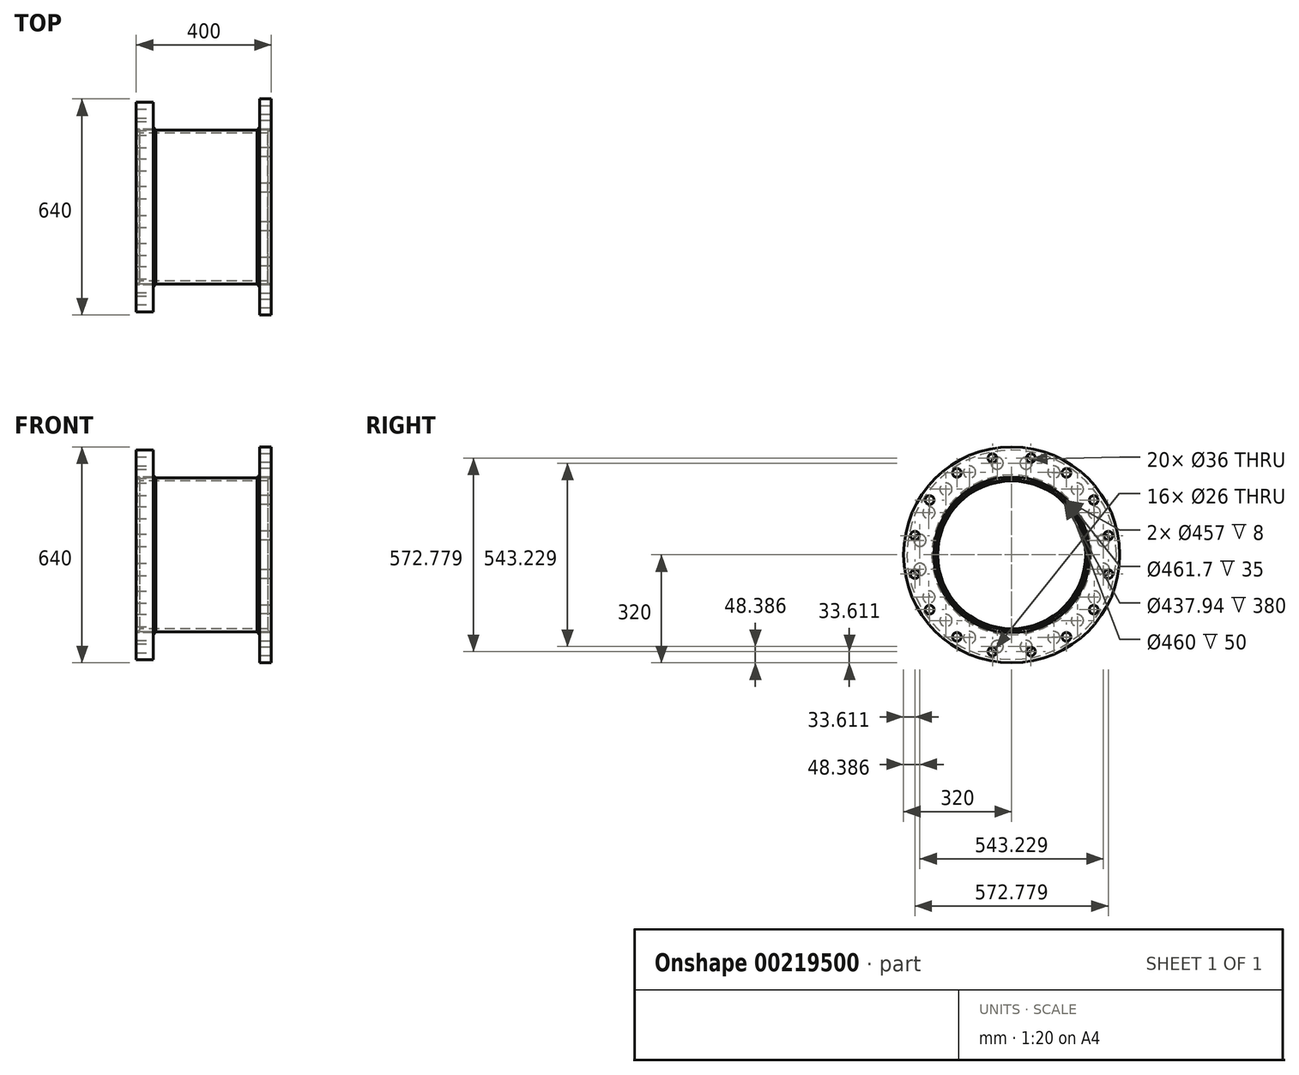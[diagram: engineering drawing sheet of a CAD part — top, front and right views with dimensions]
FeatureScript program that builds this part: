
annotation { "Feature Type Name" : "Feature", "Feature Type Description" : "" }
export const myFeature = defineFeature(function(context is Context, id is Id, definition is map)
    precondition{}
    {
        {
            var Q0;
            Q0=qCreatedBy(makeId("Front.planeOp"),FACE);
            var sketch = newSketch(context, id + "F0", { "sketchPlane" : qUnion([Q0])});
            skLineSegment(sketch, "E0", {"start": v(-189.34, 0) * mm, "end": v(169, 0) * mm, "construction": true});
            skLineSegment(sketch, "E1.bottom", {"start": v(0, 218.97) * mm, "end": v(-190, 218.97) * mm});
            skLineSegment(sketch, "E1.top", {"start": v(0, 228.5) * mm, "end": v(-190, 228.5) * mm});
            skLineSegment(sketch, "E1.left", {"start": v(0, 218.97) * mm, "end": v(0, 228.5) * mm});
            skLineSegment(sketch, "E1.right", {"start": v(-190, 218.97) * mm, "end": v(-190, 228.5) * mm});
            skLineSegment(sketch, "E2.bottom", {"start": v(-150, 230) * mm, "end": v(-200, 230) * mm});
            skLineSegment(sketch, "E2.top", {"start": v(-150, 310) * mm, "end": v(-200, 310) * mm});
            skLineSegment(sketch, "E2.left", {"start": v(-150, 230) * mm, "end": v(-150, 310) * mm});
            skLineSegment(sketch, "E2.right", {"start": v(-200, 230) * mm, "end": v(-200, 310) * mm});
            skLineSegment(sketch, "E3", {"start": v(0, 356.96) * mm, "end": v(0, -269.86) * mm, "construction": true});
            skLineSegment(sketch, "E4.MirrorCS", {"start": v(0, 228.5) * mm, "end": v(190, 228.5) * mm});
            skLineSegment(sketch, "E5.MirrorCS", {"start": v(0, 218.97) * mm, "end": v(190, 218.97) * mm});
            skLineSegment(sketch, "E6.MirrorCS", {"start": v(190, 218.97) * mm, "end": v(190, 228.5) * mm});
            skLineSegment(sketch, "E7.bottom", {"start": v(165, 230.85) * mm, "end": v(200, 230.85) * mm});
            skLineSegment(sketch, "E7.top", {"start": v(165, 320) * mm, "end": v(200, 320) * mm});
            skLineSegment(sketch, "E7.left", {"start": v(165, 230.85) * mm, "end": v(165, 320) * mm});
            skLineSegment(sketch, "E7.right", {"start": v(200, 230.85) * mm, "end": v(200, 320) * mm});
            skLineSegment(sketch, "E8", {"start": v(-198, 230) * mm, "end": v(-190, 222) * mm});
            skLineSegment(sketch, "E9", {"start": v(-190, 230) * mm, "end": v(-190, 228.5) * mm});
            skLineSegment(sketch, "E10", {"start": v(190, 228.5) * mm, "end": v(190, 230.85) * mm});
            skLineSegment(sketch, "E11", {"start": v(198, 230.85) * mm, "end": v(190, 222.85) * mm});
            skLineSegment(sketch, "E12", {"start": v(165, 230.85) * mm, "end": v(165, 228.5) * mm});
            skLineSegment(sketch, "E13", {"start": v(165, 236.5) * mm, "end": v(157, 228.5) * mm});
            skLineSegment(sketch, "E14", {"start": v(-150, 236.5) * mm, "end": v(-142, 228.5) * mm});
            skLineSegment(sketch, "E15", {"start": v(-150, 230) * mm, "end": v(-150, 228.5) * mm});
            skSolve(sketch);
        }
        {
            var Q0;
            {var subQ0=sQuery(id+"F0.wireOp",EDGE,"E2.top");Q0=makeQuery(id+"F0.imprint","IMPRINT",FACE,{"disambiguationData":[TD([[makeQuery(id+"F0.imprint","IMPRINT",EDGE,{"derivedFrom":subQ0}),1.0]])]});}
            var Q1;
            Q1=sQuery(id+"F0.wireOp",EDGE,"E0");
            revolve(context, id + "F1", {"entities" : qUnion([Q0]), "axis" : qUnion([Q1]), "revolveType" : RevolveType.FULL});
        }
        {
            var Q0;
            {var subQ0=sQuery(id+"F0.wireOp",EDGE,"E7.top");Q0=makeQuery(id+"F0.imprint","IMPRINT",FACE,{"disambiguationData":[TD([[makeQuery(id+"F0.imprint","IMPRINT",EDGE,{"derivedFrom":subQ0}),-1.0]])]});}
            var Q1;
            Q1=sQuery(id+"F0.wireOp",EDGE,"E0");
            revolve(context, id + "F2", {"entities" : qUnion([Q0]), "axis" : qUnion([Q1]), "revolveType" : RevolveType.FULL});
        }
        {
            var Q0;
            {var subQ5=sQuery(id+"F0.wireOp",EDGE,"E1.left");Q0=makeQuery(id+"F0.imprint","IMPRINT",FACE,{"disambiguationData":[TD([[makeQuery(id+"F0.imprint","IMPRINT",EDGE,{"derivedFrom":subQ5}),-1.0]])]});}
            var Q1;
            {var subQ6=sQuery(id+"F0.wireOp",EDGE,"E1.bottom");Q1=makeQuery(id+"F0.imprint","IMPRINT",FACE,{"disambiguationData":[TD([[makeQuery(id+"F0.imprint","IMPRINT",EDGE,{"derivedFrom":subQ6}),-1.0]])]});}
            var Q2;
            Q2=sQuery(id+"F0.wireOp",EDGE,"E0");
            revolve(context, id + "F3", {"entities" : qUnion([Q0, Q1]), "axis" : qUnion([Q2]), "revolveType" : RevolveType.FULL});
        }
        {
            var Q0;
            {var subQ2=sQuery(id+"F0.wireOp",EDGE,"E8");Q0=makeQuery(id+"F0.imprint","IMPRINT",FACE,{"disambiguationData":[TD([[makeQuery(id+"F0.imprint","IMPRINT",EDGE,{"derivedFrom":subQ2}),1.0]])]});}
            var Q1;
            {var subQ0=sQuery(id+"F0.wireOp",EDGE,"E14");Q1=makeQuery(id+"F0.imprint","IMPRINT",FACE,{"disambiguationData":[TD([[makeQuery(id+"F0.imprint","IMPRINT",EDGE,{"derivedFrom":subQ0}),-1.0]])]});}
            var Q2;
            {var subQ0=sQuery(id+"F0.wireOp",EDGE,"E12");Q2=makeQuery(id+"F0.imprint","IMPRINT",FACE,{"disambiguationData":[TD([[makeQuery(id+"F0.imprint","IMPRINT",EDGE,{"derivedFrom":subQ0}),-1.0]])]});}
            var Q3;
            {var subQ0=sQuery(id+"F0.wireOp",EDGE,"E10");Q3=makeQuery(id+"F0.imprint","IMPRINT",FACE,{"disambiguationData":[TD([[makeQuery(id+"F0.imprint","IMPRINT",EDGE,{"derivedFrom":subQ0}),-1.0]])]});}
            var Q4;
            Q4=sQuery(id+"F0.wireOp",EDGE,"E0");
            revolve(context, id + "F4", {"entities" : qUnion([Q0, Q1, Q2, Q3]), "axis" : qUnion([Q4]), "revolveType" : RevolveType.FULL});
        }
        {
            var Q0;
            Q0=makeQuery(id+"F1.opRevolve","SWEPT_FACE",FACE,{"disambiguationData":[OSD([sQuery(id+"F0.wireOp",EDGE,"E2.right")])]});
            var sketch = newSketch(context, id + "F5", { "sketchPlane" : qUnion([Q0])});
            skCircle(sketch, "E16.cCircle", {"center": v(0, 0) * mm, "radius": 275 * mm, "construction": true});
            skLineSegment(sketch, "E16.0", {"start": v(124.85, 245.03) * mm, "end": v(194.45, 194.45) * mm});
            skLineSegment(sketch, "E16.1", {"start": v(194.45, 194.45) * mm, "end": v(245.03, 124.85) * mm});
            skLineSegment(sketch, "E16.2", {"start": v(245.03, 124.85) * mm, "end": v(271.61, 43.02) * mm});
            skLineSegment(sketch, "E16.3", {"start": v(271.61, 43.02) * mm, "end": v(271.61, -43.02) * mm});
            skLineSegment(sketch, "E16.4", {"start": v(271.61, -43.02) * mm, "end": v(245.03, -124.85) * mm});
            skLineSegment(sketch, "E16.5", {"start": v(245.03, -124.85) * mm, "end": v(194.45, -194.45) * mm});
            skLineSegment(sketch, "E16.6", {"start": v(194.45, -194.45) * mm, "end": v(124.85, -245.03) * mm});
            skLineSegment(sketch, "E16.7", {"start": v(124.85, -245.03) * mm, "end": v(43.02, -271.61) * mm});
            skLineSegment(sketch, "E16.8", {"start": v(43.02, -271.61) * mm, "end": v(-43.02, -271.61) * mm});
            skLineSegment(sketch, "E16.9", {"start": v(-43.02, -271.61) * mm, "end": v(-124.85, -245.03) * mm});
            skLineSegment(sketch, "E16.10", {"start": v(-124.85, -245.03) * mm, "end": v(-194.45, -194.45) * mm});
            skLineSegment(sketch, "E16.11", {"start": v(-194.45, -194.45) * mm, "end": v(-245.03, -124.85) * mm});
            skLineSegment(sketch, "E16.12", {"start": v(-245.03, -124.85) * mm, "end": v(-271.61, -43.02) * mm});
            skLineSegment(sketch, "E16.13", {"start": v(-271.61, -43.02) * mm, "end": v(-271.61, 43.02) * mm});
            skLineSegment(sketch, "E16.14", {"start": v(-271.61, 43.02) * mm, "end": v(-245.03, 124.85) * mm});
            skLineSegment(sketch, "E16.15", {"start": v(-245.03, 124.85) * mm, "end": v(-194.45, 194.45) * mm});
            skLineSegment(sketch, "E16.16", {"start": v(-194.45, 194.45) * mm, "end": v(-124.85, 245.03) * mm});
            skLineSegment(sketch, "E16.17", {"start": v(-124.85, 245.03) * mm, "end": v(-43.02, 271.61) * mm});
            skLineSegment(sketch, "E16.18", {"start": v(-43.02, 271.61) * mm, "end": v(43.02, 271.61) * mm});
            skLineSegment(sketch, "E16.19", {"start": v(43.02, 271.61) * mm, "end": v(124.85, 245.03) * mm});
            skPoint(sketch, "E17", {"position": v(-124.85, 245.03) * mm});
            skPoint(sketch, "E18", {"position": v(-43.02, 271.61) * mm});
            skPoint(sketch, "E19", {"position": v(43.02, 271.61) * mm});
            skPoint(sketch, "E20", {"position": v(124.85, 245.03) * mm});
            skPoint(sketch, "E21", {"position": v(194.45, 194.45) * mm});
            skPoint(sketch, "E22", {"position": v(245.03, 124.85) * mm});
            skPoint(sketch, "E23", {"position": v(271.61, 43.02) * mm});
            skPoint(sketch, "E24", {"position": v(271.61, -43.02) * mm});
            skPoint(sketch, "E25", {"position": v(245.03, -124.85) * mm});
            skPoint(sketch, "E26", {"position": v(194.45, -194.45) * mm});
            skPoint(sketch, "E27", {"position": v(124.85, -245.03) * mm});
            skPoint(sketch, "E28", {"position": v(43.02, -271.61) * mm});
            skPoint(sketch, "E29", {"position": v(-43.02, -271.61) * mm});
            skPoint(sketch, "E30", {"position": v(-124.85, -245.03) * mm});
            skPoint(sketch, "E31", {"position": v(-194.45, -194.45) * mm});
            skPoint(sketch, "E32", {"position": v(-245.03, -124.85) * mm});
            skPoint(sketch, "E33", {"position": v(-271.61, -43.02) * mm});
            skPoint(sketch, "E34", {"position": v(-271.61, 43.02) * mm});
            skPoint(sketch, "E35", {"position": v(-245.03, 124.85) * mm});
            skPoint(sketch, "E36", {"position": v(-194.45, 194.45) * mm});
            skSolve(sketch);
        }
        {
            var Q0;
            Q0=sQuery(id+"F5.wireOp",VERTEX,"E17");
            var Q1;
            Q1=sQuery(id+"F5.wireOp",VERTEX,"E18");
            var Q2;
            Q2=sQuery(id+"F5.wireOp",VERTEX,"E19");
            var Q3;
            Q3=sQuery(id+"F5.wireOp",VERTEX,"E20");
            var Q4;
            Q4=sQuery(id+"F5.wireOp",VERTEX,"E21");
            var Q5;
            Q5=sQuery(id+"F5.wireOp",VERTEX,"E22");
            var Q6;
            Q6=sQuery(id+"F5.wireOp",VERTEX,"E23");
            var Q7;
            Q7=sQuery(id+"F5.wireOp",VERTEX,"E24");
            var Q8;
            Q8=sQuery(id+"F5.wireOp",VERTEX,"E25");
            var Q9;
            Q9=sQuery(id+"F5.wireOp",VERTEX,"E26");
            var Q10;
            Q10=sQuery(id+"F5.wireOp",VERTEX,"E27");
            var Q11;
            Q11=sQuery(id+"F5.wireOp",VERTEX,"E28");
            var Q12;
            Q12=sQuery(id+"F5.wireOp",VERTEX,"E29");
            var Q13;
            Q13=sQuery(id+"F5.wireOp",VERTEX,"E30");
            var Q14;
            Q14=sQuery(id+"F5.wireOp",VERTEX,"E31");
            var Q15;
            Q15=sQuery(id+"F5.wireOp",VERTEX,"E32");
            var Q16;
            Q16=sQuery(id+"F5.wireOp",VERTEX,"E33");
            var Q17;
            Q17=sQuery(id+"F5.wireOp",VERTEX,"E34");
            var Q18;
            Q18=sQuery(id+"F5.wireOp",VERTEX,"E35");
            var Q19;
            Q19=sQuery(id+"F5.wireOp",VERTEX,"E36");
            var Q20;
            Q20=makeQuery(id+"F1.opRevolve","SWEPT_BODY",BODY,{"disambiguationData":[OSD([sQuery(id+"F0.wireOp",EDGE,"E2.bottom"),sQuery(id+"F0.wireOp",EDGE,"E2.top"),sQuery(id+"F0.wireOp",EDGE,"E2.left"),sQuery(id+"F0.wireOp",EDGE,"E2.right")])]});
            hole(context, id + "F6", {"style" : HoleStyle.SIMPLE, "endStyle" : HoleEndStyle.BLIND, "holeDiameter" : 36 * mm, "holeDepth" : 50 * mm, "locations" : qUnion([Q0, Q1, Q2, Q3, Q4, Q5, Q6, Q7, Q8, Q9, Q10, Q11, Q12, Q13, Q14, Q15, Q16, Q17, Q18, Q19]), "scope" : qUnion([Q20])});
        }
        {
            var Q0;
            Q0=makeQuery(id+"F2.opRevolve","SWEPT_FACE",FACE,{"disambiguationData":[OSD([sQuery(id+"F0.wireOp",EDGE,"E7.right")])]});
            var sketch = newSketch(context, id + "F7", { "sketchPlane" : qUnion([Q0])});
            skCircle(sketch, "E37.cCircle", {"center": v(0, 0) * mm, "radius": 292 * mm, "construction": true});
            skLineSegment(sketch, "E37.0", {"start": v(162.23, 242.79) * mm, "end": v(242.79, 162.23) * mm});
            skLineSegment(sketch, "E37.1", {"start": v(242.79, 162.23) * mm, "end": v(286.39, 56.97) * mm});
            skLineSegment(sketch, "E37.2", {"start": v(286.39, 56.97) * mm, "end": v(286.39, -56.97) * mm});
            skLineSegment(sketch, "E37.3", {"start": v(286.39, -56.97) * mm, "end": v(242.79, -162.23) * mm});
            skLineSegment(sketch, "E37.4", {"start": v(242.79, -162.23) * mm, "end": v(162.23, -242.79) * mm});
            skLineSegment(sketch, "E37.5", {"start": v(162.23, -242.79) * mm, "end": v(56.97, -286.39) * mm});
            skLineSegment(sketch, "E37.6", {"start": v(56.97, -286.39) * mm, "end": v(-56.97, -286.39) * mm});
            skLineSegment(sketch, "E37.7", {"start": v(-56.97, -286.39) * mm, "end": v(-162.23, -242.79) * mm});
            skLineSegment(sketch, "E37.8", {"start": v(-162.23, -242.79) * mm, "end": v(-242.79, -162.23) * mm});
            skLineSegment(sketch, "E37.9", {"start": v(-242.79, -162.23) * mm, "end": v(-286.39, -56.97) * mm});
            skLineSegment(sketch, "E37.10", {"start": v(-286.39, -56.97) * mm, "end": v(-286.39, 56.97) * mm});
            skLineSegment(sketch, "E37.11", {"start": v(-286.39, 56.97) * mm, "end": v(-242.79, 162.23) * mm});
            skLineSegment(sketch, "E37.12", {"start": v(-242.79, 162.23) * mm, "end": v(-162.23, 242.79) * mm});
            skLineSegment(sketch, "E37.13", {"start": v(-162.23, 242.79) * mm, "end": v(-56.97, 286.39) * mm});
            skLineSegment(sketch, "E37.14", {"start": v(-56.97, 286.39) * mm, "end": v(56.97, 286.39) * mm});
            skLineSegment(sketch, "E37.15", {"start": v(56.97, 286.39) * mm, "end": v(162.23, 242.79) * mm});
            skPoint(sketch, "E38", {"position": v(-56.97, 286.39) * mm});
            skPoint(sketch, "E39", {"position": v(56.97, 286.39) * mm});
            skPoint(sketch, "E40", {"position": v(162.23, 242.79) * mm});
            skPoint(sketch, "E41", {"position": v(242.79, 162.23) * mm});
            skPoint(sketch, "E42", {"position": v(286.39, 56.97) * mm});
            skPoint(sketch, "E43", {"position": v(286.39, -56.97) * mm});
            skPoint(sketch, "E44", {"position": v(242.79, -162.23) * mm});
            skPoint(sketch, "E45", {"position": v(162.23, -242.79) * mm});
            skPoint(sketch, "E46", {"position": v(56.97, -286.39) * mm});
            skPoint(sketch, "E47", {"position": v(-56.97, -286.39) * mm});
            skPoint(sketch, "E48", {"position": v(-162.23, -242.79) * mm});
            skPoint(sketch, "E49", {"position": v(-242.79, -162.23) * mm});
            skPoint(sketch, "E50", {"position": v(-286.39, -56.97) * mm});
            skPoint(sketch, "E51", {"position": v(-286.39, 56.97) * mm});
            skPoint(sketch, "E52", {"position": v(-242.79, 162.23) * mm});
            skPoint(sketch, "E53", {"position": v(-162.23, 242.79) * mm});
            skSolve(sketch);
        }
        {
            var Q0;
            Q0=sQuery(id+"F7.wireOp",VERTEX,"E53");
            var Q1;
            Q1=sQuery(id+"F7.wireOp",VERTEX,"E38");
            var Q2;
            Q2=sQuery(id+"F7.wireOp",VERTEX,"E39");
            var Q3;
            Q3=sQuery(id+"F7.wireOp",VERTEX,"E40");
            var Q4;
            Q4=sQuery(id+"F7.wireOp",VERTEX,"E42");
            var Q5;
            Q5=sQuery(id+"F7.wireOp",VERTEX,"E43");
            var Q6;
            Q6=sQuery(id+"F7.wireOp",VERTEX,"E41");
            var Q7;
            Q7=sQuery(id+"F7.wireOp",VERTEX,"E44");
            var Q8;
            Q8=sQuery(id+"F7.wireOp",VERTEX,"E45");
            var Q9;
            Q9=sQuery(id+"F7.wireOp",VERTEX,"E46");
            var Q10;
            Q10=sQuery(id+"F7.wireOp",VERTEX,"E47");
            var Q11;
            Q11=sQuery(id+"F7.wireOp",VERTEX,"E48");
            var Q12;
            Q12=sQuery(id+"F7.wireOp",VERTEX,"E50");
            var Q13;
            Q13=sQuery(id+"F7.wireOp",VERTEX,"E49");
            var Q14;
            Q14=sQuery(id+"F7.wireOp",VERTEX,"E52");
            var Q15;
            Q15=sQuery(id+"F7.wireOp",VERTEX,"E51");
            var Q16;
            Q16=makeQuery(id+"F2.opRevolve","SWEPT_BODY",BODY,{"disambiguationData":[OSD([sQuery(id+"F0.wireOp",EDGE,"E7.bottom"),sQuery(id+"F0.wireOp",EDGE,"E7.top"),sQuery(id+"F0.wireOp",EDGE,"E7.left"),sQuery(id+"F0.wireOp",EDGE,"E7.right")])]});
            hole(context, id + "F8", {"style" : HoleStyle.SIMPLE, "endStyle" : HoleEndStyle.BLIND, "holeDiameter" : 26 * mm, "holeDepth" : 50 * mm, "locations" : qUnion([Q0, Q1, Q2, Q3, Q4, Q5, Q6, Q7, Q8, Q9, Q10, Q11, Q12, Q13, Q14, Q15]), "scope" : qUnion([Q16])});
        }
    });
